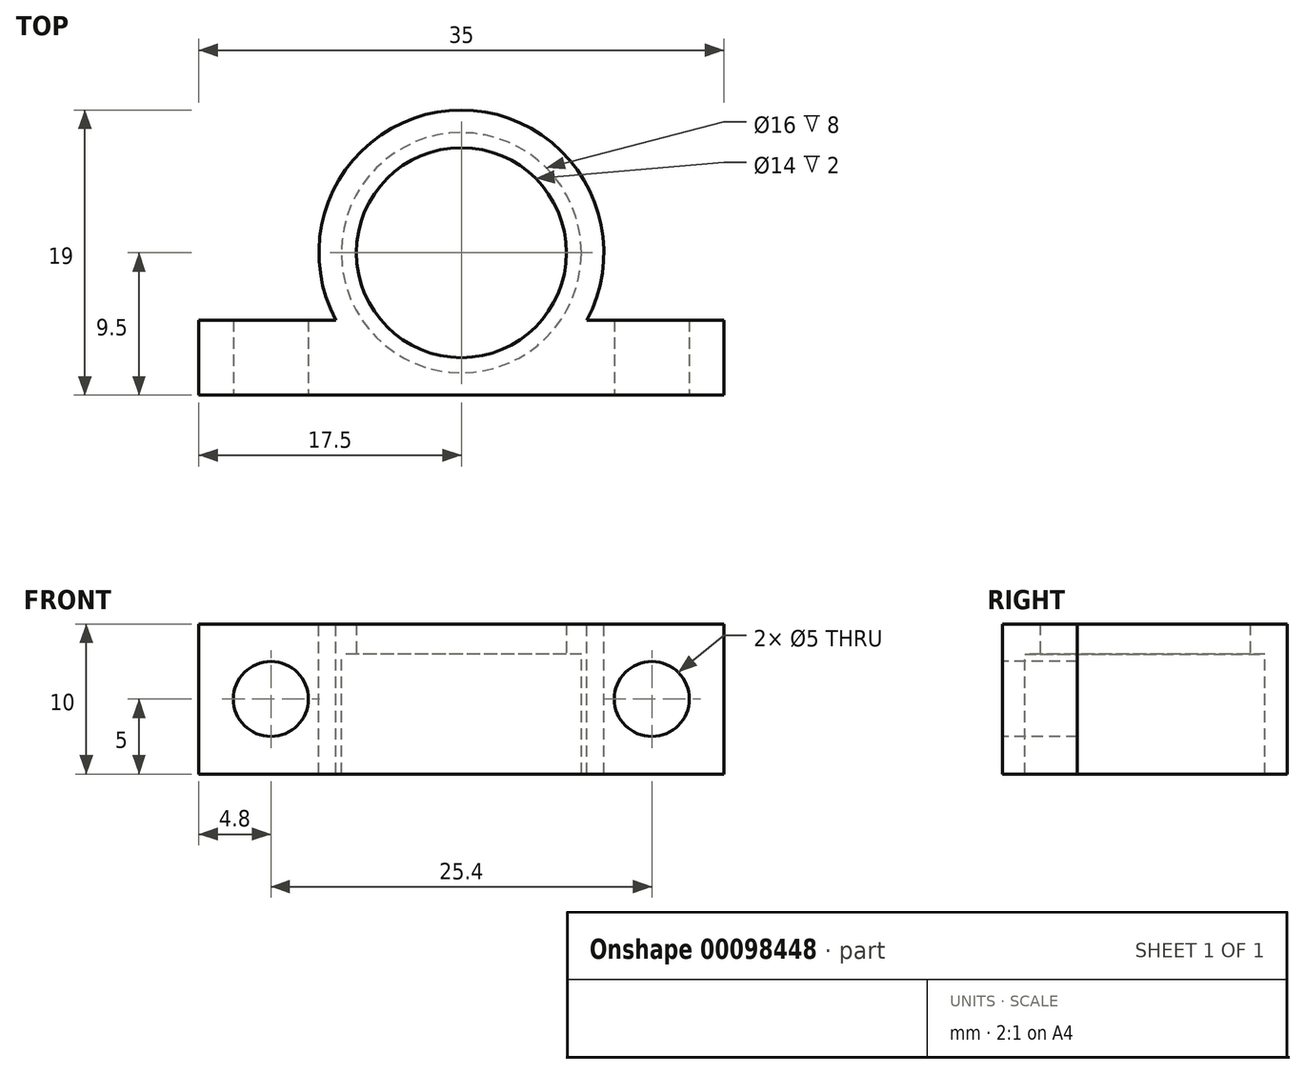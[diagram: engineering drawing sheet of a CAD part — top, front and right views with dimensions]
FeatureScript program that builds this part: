
annotation { "Feature Type Name" : "Feature", "Feature Type Description" : "" }
export const myFeature = defineFeature(function(context is Context, id is Id, definition is map)
    precondition{}
    {
        {
            var Q0;
            Q0=qCreatedBy(makeId("Top.planeOp"),FACE);
            var sketch = newSketch(context, id + "F0", { "sketchPlane" : qUnion([Q0])});
            skCircle(sketch, "E0", {"center": v(0, 0) * mm, "radius": 8 * mm});
            skArc(sketch, "E1", {"start": v(8.37, -4.5) * mm, "mid": v(0, 9.5) * mm, "end": v(-8.37, -4.5) * mm});
            skLineSegment(sketch, "E2", {"start": v(0, -9.5) * mm, "end": v(-17.5, -9.5) * mm});
            skLineSegment(sketch, "E3.MirrorCS", {"start": v(0, -9.5) * mm, "end": v(17.5, -9.5) * mm});
            skLineSegment(sketch, "E4", {"start": v(-17.5, -9.5) * mm, "end": v(-17.5, -4.5) * mm});
            skLineSegment(sketch, "E5", {"start": v(-17.5, -4.5) * mm, "end": v(-8.37, -4.5) * mm});
            skLineSegment(sketch, "E6.MirrorCS", {"start": v(17.5, -4.5) * mm, "end": v(8.37, -4.5) * mm});
            skLineSegment(sketch, "E7.MirrorCS", {"start": v(17.5, -9.5) * mm, "end": v(17.5, -4.5) * mm});
            skPoint(sketch, "E8.orphan", {"position": v(0, -4.5) * mm});
            skSolve(sketch);
        }
        {
            var Q0;
            Q0=makeQuery(id+"F0.imprint","IMPRINT",FACE,{"disambiguationData":[TD([[makeQuery(id+"F0.imprint","IMPRINT",EDGE,{"derivedFrom":sQuery(id+"F0.wireOp",EDGE,"E0")}),-1.0]])]});
            extrude(context, id + "F1", {"entities" : qUnion([Q0]), "oppositeDirection" : true, "depth" : 8 * mm});
        }
        {
            var Q0;
            Q0=qCreatedBy(makeId("Top.planeOp"),FACE);
            var sketch = newSketch(context, id + "F2", { "sketchPlane" : qUnion([Q0])});
            skCircle(sketch, "E9", {"center": v(0, 0) * mm, "radius": 7 * mm});
            skArc(sketch, "E10", {"start": v(8.37, -4.5) * mm, "mid": v(0, 9.5) * mm, "end": v(-8.37, -4.5) * mm});
            skLineSegment(sketch, "E11", {"start": v(0, -4.5) * mm, "end": v(0, -7) * mm});
            skLineSegment(sketch, "E12", {"start": v(0, -9.5) * mm, "end": v(17.5, -9.5) * mm});
            skLineSegment(sketch, "E13", {"start": v(17.5, -9.5) * mm, "end": v(17.5, -4.5) * mm});
            skLineSegment(sketch, "E14", {"start": v(17.5, -4.5) * mm, "end": v(8.37, -4.5) * mm});
            skLineSegment(sketch, "E15.MirrorCS", {"start": v(-17.5, -4.5) * mm, "end": v(-8.37, -4.5) * mm});
            skLineSegment(sketch, "E16.MirrorCS", {"start": v(-17.5, -9.5) * mm, "end": v(-17.5, -4.5) * mm});
            skLineSegment(sketch, "E17.MirrorCS", {"start": v(0, -9.5) * mm, "end": v(-17.5, -9.5) * mm});
            skSolve(sketch);
        }
        {
            var Q0;
            Q0 = qSketchRegion(id + "F2", true);
            var Q1;
            Q1=makeQuery(id+"F0.imprint","IMPRINT",FACE,{"disambiguationData":[TD([[makeQuery(id+"F0.imprint","IMPRINT",EDGE,{"derivedFrom":sQuery(id+"F0.wireOp",EDGE,"E0")}),-1.0]])]});
            extrude(context, id + "F3", {"entities" : qUnion([Q0, Q1]), "operationType" : NewBodyOperationType.ADD, "depth" : 2 * mm});
        }
        {
            var Q0;
            {var subQ0=sQuery(id+"F0.wireOp",EDGE,"E3.MirrorCS");var subQ1=sQuery(id+"F0.wireOp",EDGE,"E2");Q0=makeQuery(id+"F3.boolean.opBoolean","MERGE",FACE,{"derivedFrom":[makeQuery(id+"F1.opExtrude","SWEPT_FACE",FACE,{"disambiguationData":[OSD([subQ1,subQ0])]}),makeQuery(id+"F3.opExtrude","SWEPT_FACE",FACE,{"disambiguationData":[OSD([subQ1,subQ0])]})]});}
            var sketch = newSketch(context, id + "F4", { "sketchPlane" : qUnion([Q0])});
            skLineSegment(sketch, "E18", {"start": v(0, 0) * mm, "end": v(0, 2) * mm});
            skCircle(sketch, "E19", {"center": v(-12.7, -3) * mm, "radius": 2.5 * mm});
            skCircle(sketch, "E20", {"center": v(12.7, -3) * mm, "radius": 2.5 * mm});
            skSolve(sketch);
        }
        {
            var Q0;
            Q0 = qSketchRegion(id + "F4", true);
            extrude(context, id + "F5", {"entities" : qUnion([Q0]), "operationType" : NewBodyOperationType.REMOVE, "oppositeDirection" : true, "depth" : 25.4 * mm});
        }
    });
